# Revit family: QF_LANCER_FS30
name_source: partatom
category: Specialty Equipment
revit_build: Autodesk Revit Architecture 2012 (Build: 20110916_2132(x64)
units: mm (PartAtom-declared; Revit-internal decimal feet)

## types (1)
- QF_LANCER_FS30
    Apparent Power = 805 VA
    Cold Water Connection Height = 0"
    Cold Water Maximum Pressure = 0.00 psi
    Cold Water Minimum Pressure = 0.00 psi
    Cold Water Size = 0"
    Conn Conduit = Yes
    Cycle = 60 Hz
    Description = ICE BEVERAGE DISPENSER
    Elec Conn Connection Height = 0"
    Elec Conn RI Height = 0"
    FL Amps = 7 A
    Indirect Waste Connection Height = 0"
    Indirect Waste Size = 1"
    Manufacturer = LANCER
    Max Overcurrent Protection = 0 A
    Min Ckt Ampacity = 0 A
    Model = FS30
    Number of Poles = 1
    Phase = 1
    URL = www.lancercorp.com
    URL Cutsheet = www.lancercorp.com
    Volts = 115 V
    Watts = 0 W
    Weight in Pounds = 320

## geometry (parser evidence)
native form markers: Blend x2, Sweep x3
no freeform markers — native parametric forms only
